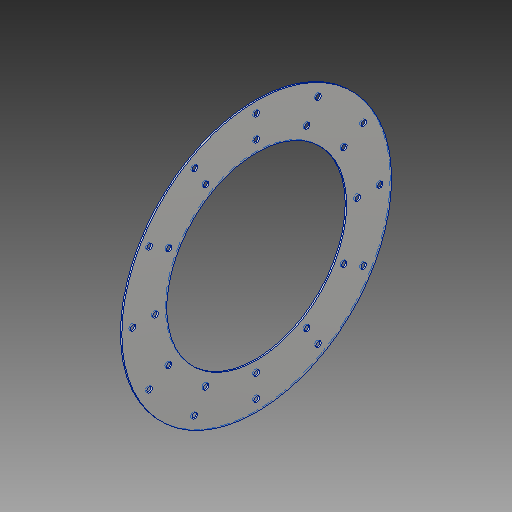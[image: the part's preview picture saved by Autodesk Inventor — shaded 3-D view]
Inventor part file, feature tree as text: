
AUTODESK INVENTOR PART (.ipt)
format: ipt  version: 2019 (Build 230136000, 136)  size: 142,848 bytes
history: native  units: in
note: dims shown in document units (in); Inventor stores cm internally (conversion verified against a paired STEP export)
features: extrude x2, sketch x2
ambient origin geometry x8: Origin, YZ Plane, XZ Plane, XY Plane, X Axis, Y Axis, Z Axis, Center Point
bodies: Solid1 (feature_tree)
feature tree (4):
  extrude  "Extrusion1"  Depth=0.5in
  extrude  "Extrusion2"  Depth=0.0625in
  sketch  "Sketch1"  dims[d0=12.0in d1=0.5in]
  sketch  "Sketch2"  dims[d2=1.0in d3=0.25in d4=4.7244in d6=360.0deg d8=0.0625in d9=0.0in d10=8.0in d11=1.0in d12=0.0in]
